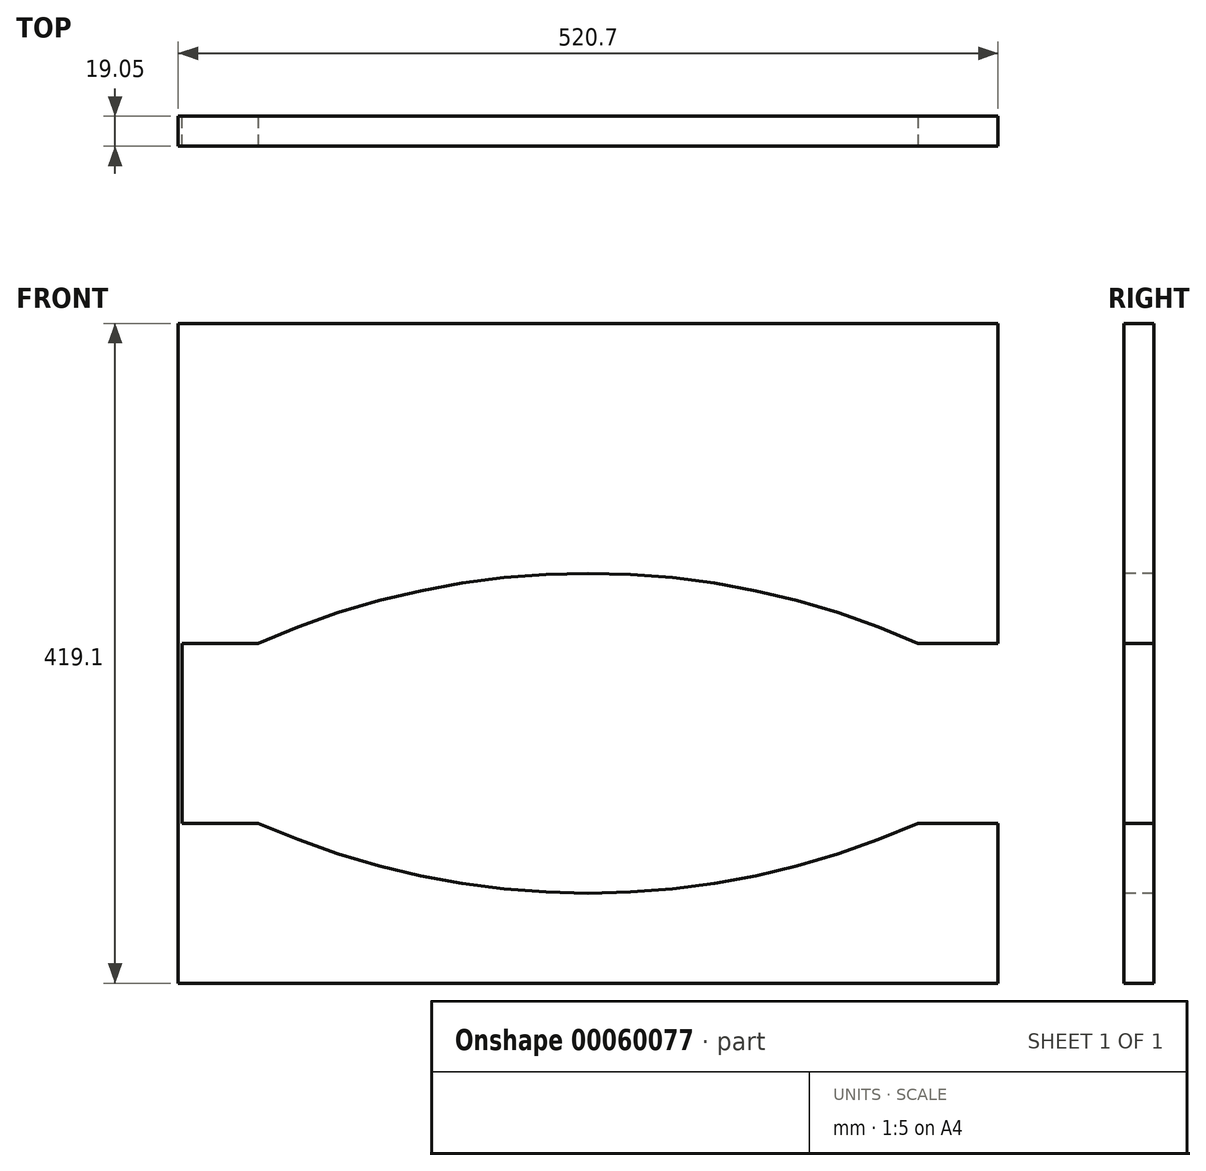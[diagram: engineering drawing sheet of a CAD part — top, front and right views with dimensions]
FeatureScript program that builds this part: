
annotation { "Feature Type Name" : "Feature", "Feature Type Description" : "" }
export const myFeature = defineFeature(function(context is Context, id is Id, definition is map)
    precondition{}
    {
        {
            var Q0;
            Q0=qCreatedBy(makeId("Front.planeOp"),FACE);
            var sketch = newSketch(context, id + "F0", { "sketchPlane" : qUnion([Q0])});
            skLineSegment(sketch, "E0.bottom", {"start": v(-260.35, -209.55) * mm, "end": v(260.35, -209.55) * mm});
            skLineSegment(sketch, "E0.top", {"start": v(-260.35, 209.55) * mm, "end": v(260.35, 209.55) * mm});
            skLineSegment(sketch, "E0.left", {"start": v(-260.35, -209.55) * mm, "end": v(-260.35, 209.55) * mm});
            skLineSegment(sketch, "E0.right", {"start": v(260.35, -209.55) * mm, "end": v(260.35, 209.55) * mm});
            skLineSegment(sketch, "E1", {"start": v(-260.35, 209.55) * mm, "end": v(260.35, -209.55) * mm, "construction": true});
            skSolve(sketch);
        }
        {
            var Q0;
            Q0=qSketchRegion(id+"F0",true);
            extrude(context, id + "F1", {"entities" : qUnion([Q0]), "oppositeDirection" : true, "depth" : 19.05 * mm});
        }
        {
            var Q0;
            {var subQ0=sQuery(id+"F0.wireOp",EDGE,"E0.left");var subQ1=sQuery(id+"F0.wireOp",EDGE,"E0.top");var subQ2=sQuery(id+"F0.wireOp",EDGE,"E0.bottom");var subQ3=sQuery(id+"F0.wireOp",EDGE,"E0.right");Q0=makeQuery(id+"F2.boolean.opBoolean","SPLIT",FACE,{"disambiguationData":[TD([makeQuery(id+"F1.opExtrude","SWEPT_FACE",FACE,{"disambiguationData":[OSD([subQ2])]})])],"derivedFrom":makeQuery(id+"F1.opExtrude","CAP_FACE",FACE,{"disambiguationData":[OSD([subQ2,subQ1,subQ0,subQ3])],"isStart":true})});}
            var sketch = newSketch(context, id + "F3", { "sketchPlane" : qUnion([Q0])});
            skLineSegment(sketch, "E2.bottom", {"start": v(-260.35, 6.35) * mm, "end": v(260.35, 6.35) * mm});
            skLineSegment(sketch, "E2.top", {"start": v(-260.35, -107.95) * mm, "end": v(260.35, -107.95) * mm});
            skLineSegment(sketch, "E2.left", {"start": v(-260.35, 6.35) * mm, "end": v(-260.35, -107.95) * mm});
            skLineSegment(sketch, "E2.right", {"start": v(260.35, 6.35) * mm, "end": v(260.35, -107.95) * mm});
            skSolve(sketch);
        }
        {
            var Q0;
            Q0 = qSketchRegion(id + "F3", true);
            extrude(context, id + "F4", {"entities" : qUnion([Q0]), "operationType" : NewBodyOperationType.REMOVE, "oppositeDirection" : true, "depth" : 25.4 * mm});
        }
        {
            var Q0;
            {var subQ19=sQuery(id+"F0.wireOp",EDGE,"E0.top");var subQ20=makeQuery(id+"F1.opExtrude","SWEPT_FACE",FACE,{"disambiguationData":[OSD([subQ19])]});var subQ36=sQuery(id+"F0.wireOp",EDGE,"E0.left");var subQ41=sQuery(id+"F0.wireOp",EDGE,"E0.right");var subQ66=sQuery(id+"F0.wireOp",EDGE,"E0.bottom");Q0=makeQuery(id+"F4.boolean.opBoolean","SPLIT",FACE,{"disambiguationData":[TD([subQ20])],"derivedFrom":makeQuery(id+"F2.boolean.opBoolean","SPLIT",FACE,{"disambiguationData":[TD([makeQuery(id+"F1.opExtrude","SWEPT_FACE",FACE,{"disambiguationData":[OSD([subQ66])]})])],"derivedFrom":makeQuery(id+"F1.opExtrude","CAP_FACE",FACE,{"disambiguationData":[OSD([subQ66,subQ19,subQ36,subQ41])],"isStart":true})})});}
            var sketch = newSketch(context, id + "F5", { "sketchPlane" : qUnion([Q0])});
            skArc(sketch, "E3", {"start": v(-260.35, 158.75) * mm, "mid": v(-224.43, 173.63) * mm, "end": v(-209.55, 209.55) * mm, "construction": true});
            skArc(sketch, "E4", {"start": v(209.55, 209.55) * mm, "mid": v(224.43, 173.63) * mm, "end": v(260.35, 158.75) * mm, "construction": true});
            skArc(sketch, "E5", {"start": v(307.5, -50.8) * mm, "mid": v(0, 50.8) * mm, "end": v(-307.5, -50.8) * mm});
            skArc(sketch, "E6", {"start": v(-307.5, -50.8) * mm, "mid": v(0, -152.4) * mm, "end": v(307.5, -50.8) * mm});
            skLineSegment(sketch, "E7", {"start": v(-209.55, 6.35) * mm, "end": v(-209.55, -107.95) * mm, "construction": true});
            skLineSegment(sketch, "E8", {"start": v(209.55, 6.35) * mm, "end": v(209.55, -107.95) * mm, "construction": true});
            skLineSegment(sketch, "E9", {"start": v(-260.35, 158.75) * mm, "end": v(-260.35, 209.55) * mm, "construction": true});
            skLineSegment(sketch, "E10", {"start": v(-260.35, 209.55) * mm, "end": v(-209.55, 209.55) * mm, "construction": true});
            skLineSegment(sketch, "E11", {"start": v(209.55, 209.55) * mm, "end": v(260.35, 209.55) * mm, "construction": true});
            skLineSegment(sketch, "E12", {"start": v(260.35, 209.55) * mm, "end": v(260.35, 158.75) * mm, "construction": true});
            skSolve(sketch);
        }
        {
            var Q0;
            Q0 = qSketchRegion(id + "F5", true);
            extrude(context, id + "F6", {"entities" : qUnion([Q0]), "operationType" : NewBodyOperationType.REMOVE, "oppositeDirection" : true, "depth" : 25.4 * mm});
        }
        {
            var Q0;
            {var subQ19=sQuery(id+"F0.wireOp",EDGE,"E0.top");var subQ20=makeQuery(id+"F1.opExtrude","SWEPT_FACE",FACE,{"disambiguationData":[OSD([subQ19])]});var subQ36=sQuery(id+"F0.wireOp",EDGE,"E0.left");var subQ41=sQuery(id+"F0.wireOp",EDGE,"E0.right");var subQ66=sQuery(id+"F0.wireOp",EDGE,"E0.bottom");Q0=makeQuery(id+"F4.boolean.opBoolean","SPLIT",FACE,{"disambiguationData":[TD([subQ20])],"derivedFrom":makeQuery(id+"F2.boolean.opBoolean","SPLIT",FACE,{"disambiguationData":[TD([makeQuery(id+"F1.opExtrude","SWEPT_FACE",FACE,{"disambiguationData":[OSD([subQ66])]})])],"derivedFrom":makeQuery(id+"F1.opExtrude","CAP_FACE",FACE,{"disambiguationData":[OSD([subQ66,subQ19,subQ36,subQ41])],"isStart":true})})});}
            var sketch = newSketch(context, id + "F7", { "sketchPlane" : qUnion([Q0])});
            skLineSegment(sketch, "E13.bottom", {"start": v(-260.35, 93.5) * mm, "end": v(-257.81, 93.5) * mm});
            skLineSegment(sketch, "E13.top", {"start": v(-260.35, -149.9) * mm, "end": v(-257.81, -149.9) * mm});
            skLineSegment(sketch, "E13.left", {"start": v(-260.35, 93.5) * mm, "end": v(-260.35, -149.9) * mm});
            skLineSegment(sketch, "E13.right", {"start": v(-257.81, 93.5) * mm, "end": v(-257.81, -149.9) * mm});
            skSolve(sketch);
        }
        {
            var Q0;
            Q0 = qSketchRegion(id + "F7", true);
            var Q1;
            {var subQ0=sQuery(id+"F0.wireOp",EDGE,"E0.top");var subQ1=sQuery(id+"F0.wireOp",EDGE,"E0.left");var subQ2=sQuery(id+"F0.wireOp",EDGE,"E0.right");Q1=makeQuery(id+"F4.boolean.opBoolean","SPLIT",FACE,{"disambiguationData":[TD([makeQuery(id+"F1.opExtrude","SWEPT_FACE",FACE,{"disambiguationData":[OSD([subQ0])]})])],"derivedFrom":makeQuery(id+"F1.opExtrude","CAP_FACE",FACE,{"disambiguationData":[OSD([sQuery(id+"F0.wireOp",EDGE,"E0.bottom"),subQ0,subQ1,subQ2])],"isStart":false})});}
            extrude(context, id + "F8", {"entities" : qUnion([Q0]), "operationType" : NewBodyOperationType.ADD, "endBound" : BoundingType.UP_TO_SURFACE, "oppositeDirection" : true, "endBoundEntityFace" : qUnion([Q1]), "depth" : 25.4 * mm});
        }
    });
